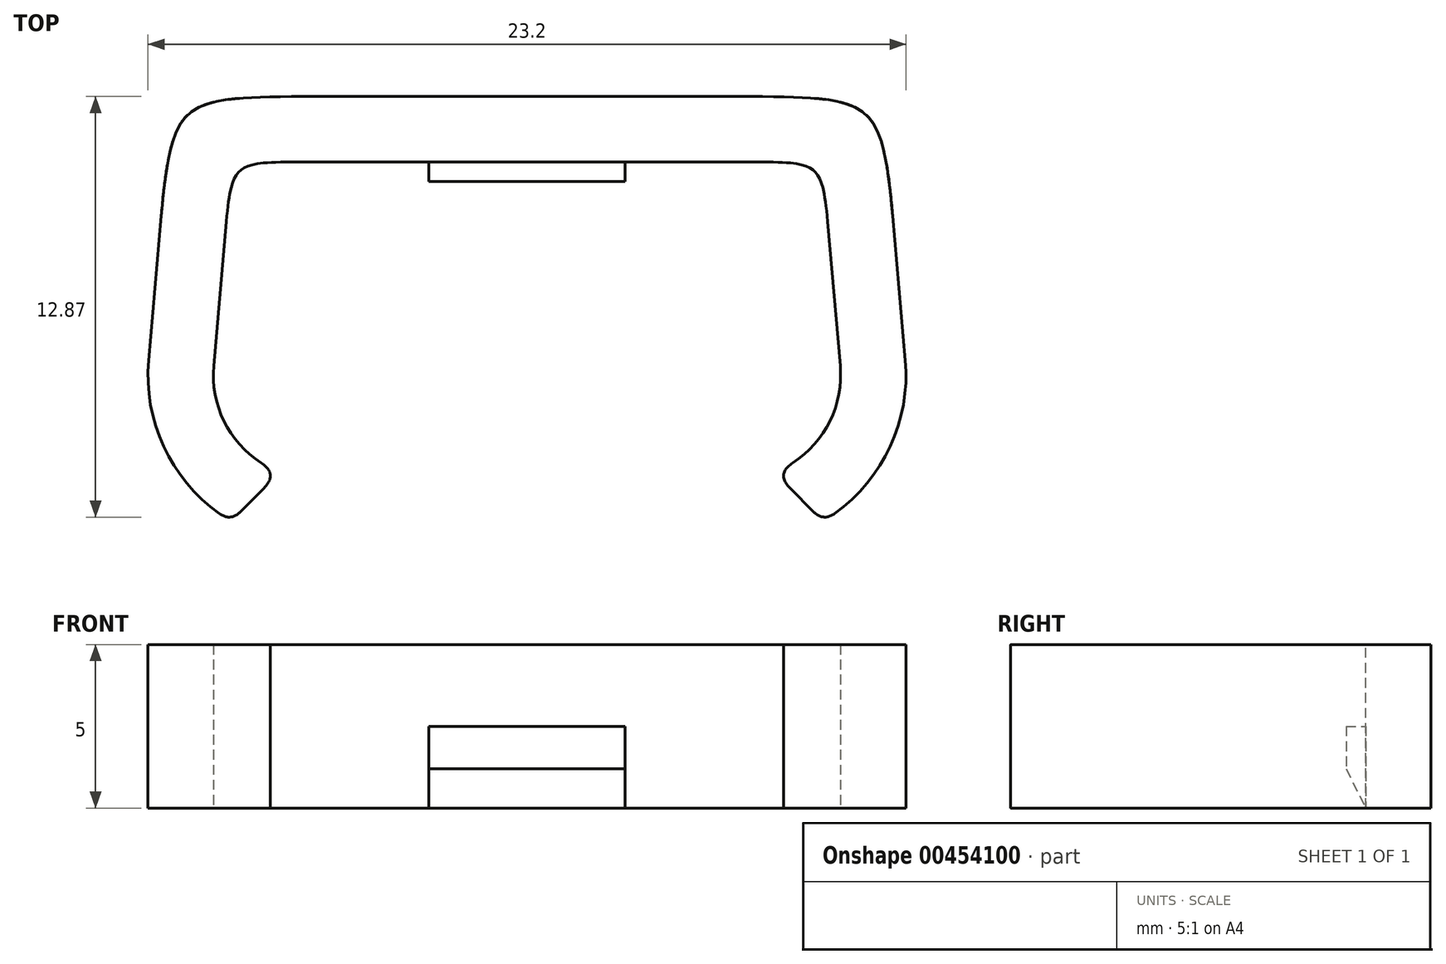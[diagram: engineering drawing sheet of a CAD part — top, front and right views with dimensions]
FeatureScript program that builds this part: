
annotation { "Feature Type Name" : "Feature", "Feature Type Description" : "" }
export const myFeature = defineFeature(function(context is Context, id is Id, definition is map)
    precondition{}
    {
        {
            var Q0;
            Q0=qCreatedBy(makeId("Top.planeOp"),FACE);
            var sketch = newSketch(context, id + "F0", { "sketchPlane" : qUnion([Q0])});
            skLineSegment(sketch, "E0", {"start": v(0, 0) * mm, "end": v(7.15, 0) * mm});
            skLineSegment(sketch, "E1", {"start": v(7.15, 0) * mm, "end": v(7.15, -3) * mm});
            skArc(sketch, "E2", {"start": v(8.15, -9.67) * mm, "mid": v(9.96, -5.99) * mm, "end": v(7.15, -3) * mm});
            skLineSegment(sketch, "E3", {"start": v(7.15, -3) * mm, "end": v(0, -3) * mm, "construction": true});
            skLineSegment(sketch, "E4", {"start": v(10, -6.52) * mm, "end": v(10, 0) * mm, "construction": true});
            skLineSegment(sketch, "E5", {"start": v(10, 0) * mm, "end": v(7.15, 0) * mm, "construction": true});
            skSolve(sketch);
        }
        {
            var Q0;
            Q0=qCreatedBy(makeId("Top.planeOp"),FACE);
            var sketch = newSketch(context, id + "F1", { "sketchPlane" : qUnion([Q0])});
            skArc(sketch, "E6", {"start": v(-54.7, 8.13) * mm, "mid": v(0, -13.5) * mm, "end": v(54.7, 8.13) * mm});
            skLineSegment(sketch, "E7", {"start": v(0, 66.5) * mm, "end": v(0, 0) * mm, "construction": true});
            skLineSegment(sketch, "E8", {"start": v(0, 0) * mm, "end": v(0, -13.5) * mm, "construction": true});
            skArc(sketch, "E9", {"start": v(-43.93, 4.75) * mm, "mid": v(0, -13.5) * mm, "end": v(43.93, 4.75) * mm, "construction": true});
            skSolve(sketch);
        }
        {
            var Q0;
            Q0=qCreatedBy(makeId("Top.planeOp"),FACE);
            var sketch = newSketch(context, id + "F2", { "sketchPlane" : qUnion([Q0])});
            skLineSegment(sketch, "E10", {"start": v(0, 0) * mm, "end": v(0, 2) * mm});
            skLineSegment(sketch, "E11", {"start": v(0, 2) * mm, "end": v(10.87, 2) * mm});
            skLineSegment(sketch, "E12", {"start": v(9.06, -10.99) * mm, "end": v(7.57, -9.5) * mm});
            skLineSegment(sketch, "E13", {"start": v(0, 0) * mm, "end": v(9.04, 0) * mm});
            skLineSegment(sketch, "E14", {"start": v(9.04, 0) * mm, "end": v(9.59, -6.24) * mm});
            skArc(sketch, "E15", {"start": v(7.57, -9.5) * mm, "mid": v(9.12, -8.2) * mm, "end": v(9.59, -6.24) * mm});
            skLineSegment(sketch, "E16", {"start": v(10.87, 2) * mm, "end": v(11.58, -6.07) * mm});
            skArc(sketch, "E17", {"start": v(9.06, -10.99) * mm, "mid": v(11.03, -8.9) * mm, "end": v(11.58, -6.07) * mm});
            skSolve(sketch);
        }
        {
            var Q0;
            Q0 = qSketchRegion(id + "F2", true);
            extrude(context, id + "F3", {"entities" : qUnion([Q0]), "depth" : 5 * mm});
        }
        {
            var Q0;
            Q0=makeQuery(id+"F3.opExtrude","SWEPT_EDGE",EDGE,{"disambiguationData":[OSD([sQuery(id+"F2.wireOp",EDGE,"E13"),sQuery(id+"F2.wireOp",EDGE,"E14")])]});
            fillet(context, id + "F4", {"entities" : qUnion([Q0]), "radius" : 2 * mm, "tangentPropagation" : true, "rho" : .7, "crossSection" : FilletCrossSection.CONIC, "allowEdgeOverflow" : false});
        }
        {
            var Q0;
            Q0=makeQuery(id+"F3.opExtrude","SWEPT_EDGE",EDGE,{"disambiguationData":[OSD([sQuery(id+"F2.wireOp",EDGE,"E11"),sQuery(id+"F2.wireOp",EDGE,"E16")])]});
            fillet(context, id + "F5", {"entities" : qUnion([Q0]), "radius" : 4 * mm, "tangentPropagation" : true, "rho" : .7, "crossSection" : FilletCrossSection.CONIC, "allowEdgeOverflow" : false});
        }
        {
            var Q0;
            Q0=makeQuery(id+"F3.opExtrude","SWEPT_FACE",FACE,{"disambiguationData":[OSD([sQuery(id+"F2.wireOp",EDGE,"E13")])]});
            var sketch = newSketch(context, id + "F6", { "sketchPlane" : qUnion([Q0])});
            skLineSegment(sketch, "E18.bottom", {"start": v(0, 2.5) * mm, "end": v(3, 2.5) * mm});
            skLineSegment(sketch, "E18.top", {"start": v(0, 0) * mm, "end": v(3, 0) * mm});
            skLineSegment(sketch, "E18.left", {"start": v(0, 2.5) * mm, "end": v(0, 0) * mm});
            skLineSegment(sketch, "E18.right", {"start": v(3, 2.5) * mm, "end": v(3, 0) * mm});
            skSolve(sketch);
        }
        {
            var Q0;
            Q0 = qSketchRegion(id + "F6", true);
            extrude(context, id + "F7", {"entities" : qUnion([Q0]), "operationType" : NewBodyOperationType.ADD, "depth" : 0.6 * mm});
        }
        {
            var Q0;
            Q0=makeQuery(id+"F7.opExtrude","CAP_EDGE",EDGE,{"disambiguationData":[OSD([sQuery(id+"F6.wireOp",EDGE,"E18.top")])],"isStart":false});
            chamfer(context, id + "F8", {"entities" : qUnion([Q0]), "chamferType" : ChamferType.TWO_OFFSETS, "width1" : 1.2 * mm, "oppositeDirection" : false, "width2" : .6 * mm, "tangentPropagation" : true});
        }
        {
            var Q0;
            Q0=qCreatedBy(makeId("Top.planeOp"),FACE);
            var sketch = newSketch(context, id + "F9", { "sketchPlane" : qUnion([Q0])});
            skArc(sketch, "E19", {"start": v(9.06, -10.99) * mm, "mid": v(11.06, -12.2) * mm, "end": v(13.4, -12.37) * mm});
            skArc(sketch, "E20", {"start": v(13.4, -12.37) * mm, "mid": v(15.74, -11.94) * mm, "end": v(18.07, -11.43) * mm});
            skLineSegment(sketch, "E21", {"start": v(18.07, -11.43) * mm, "end": v(18.26, -10.36) * mm});
            skArc(sketch, "E22", {"start": v(13.22, -11.39) * mm, "mid": v(15.75, -10.91) * mm, "end": v(18.26, -10.36) * mm});
            skArc(sketch, "E23", {"start": v(9.88, -10.39) * mm, "mid": v(11.43, -11.28) * mm, "end": v(13.22, -11.39) * mm});
            skLineSegment(sketch, "E24", {"start": v(9.88, -10.39) * mm, "end": v(9.06, -10.99) * mm});
            skSolve(sketch);
        }
        {
            var Q0;
            Q0=makeQuery(id+"F3.opExtrude","SWEPT_EDGE",EDGE,{"disambiguationData":[OSD([sQuery(id+"F2.wireOp",EDGE,"E12"),sQuery(id+"F2.wireOp",EDGE,"E15")])]});
            var Q1;
            Q1=makeQuery(id+"F3.opExtrude","SWEPT_EDGE",EDGE,{"disambiguationData":[OSD([sQuery(id+"F2.wireOp",EDGE,"E12"),sQuery(id+"F2.wireOp",EDGE,"E17")])]});
            fillet(context, id + "F10", {"entities" : qUnion([Q0, Q1]), "radius" : .5 * mm, "tangentPropagation" : true, "rho" : .5, "crossSection" : FilletCrossSection.CONIC, "allowEdgeOverflow" : false});
        }
        {
            var Q0;
            Q0=makeQuery(id+"F3.opExtrude","SWEPT_BODY",BODY,{"disambiguationData":[OSD([sQuery(id+"F2.wireOp",EDGE,"E10"),sQuery(id+"F2.wireOp",EDGE,"E11"),sQuery(id+"F2.wireOp",EDGE,"E12"),sQuery(id+"F2.wireOp",EDGE,"E13"),sQuery(id+"F2.wireOp",EDGE,"E14"),sQuery(id+"F2.wireOp",EDGE,"E15"),sQuery(id+"F2.wireOp",EDGE,"E16"),sQuery(id+"F2.wireOp",EDGE,"E17")])]});
            var Q1;
            Q1=makeQuery(id+"F7.boolean.opBoolean","MERGE",FACE,{"derivedFrom":[makeQuery(id+"F3.opExtrude","SWEPT_FACE",FACE,{"disambiguationData":[OSD([sQuery(id+"F2.wireOp",EDGE,"E10")])]}),makeQuery(id+"F7.opExtrude","SWEPT_FACE",FACE,{"disambiguationData":[OSD([sQuery(id+"F6.wireOp",EDGE,"E18.left")])]})]});
            mirror(context, id + "F11", {"operationType" : NewBodyOperationType.ADD, "entities" : qUnion([Q0]), "mirrorPlane" : qUnion([Q1])});
        }
    });
